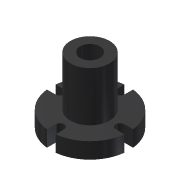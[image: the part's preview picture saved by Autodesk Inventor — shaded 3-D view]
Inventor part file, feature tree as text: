
AUTODESK INVENTOR PART (.ipt)
format: ipt  version: 2014 (Build 180170000, 170)  size: 113,664 bytes
history: native  units: mm
features: extrude x3, sketch x3, pattern_circular x1
ambient origin geometry x8: Origin, YZ Plane, XZ Plane, XY Plane, X Axis, Y Axis, Z Axis, Center Point
bodies: Solid1 (feature_tree)
feature tree (7):
  extrude  "Extrusion1"  Depth=8.1mm
  extrude  "Extrusion2"  Depth=6.46mm
  extrude  "Extrusion3"  Depth=3.5mm
  pattern_circular  "Circular Pattern1"  [2 undecoded]
  sketch  "Sketch1"  dims[d0=31.5mm d1=8.1mm]
  sketch  "Sketch2"  dims[d2=6.46mm d3=0.0mm d4=15.8mm]
  sketch  "Sketch3"  dims[d5=20.0mm d6=0.0mm d7=3.5mm d8=3.5mm d9=20.0mm d10=0.0mm d11=40.0mm d12=360.0deg]
note: 2 required parameter values undecoded (feature->parameter linkage not recoverable at this tier; creation-order binding heuristic only, values carry confidence <= 0.55)
